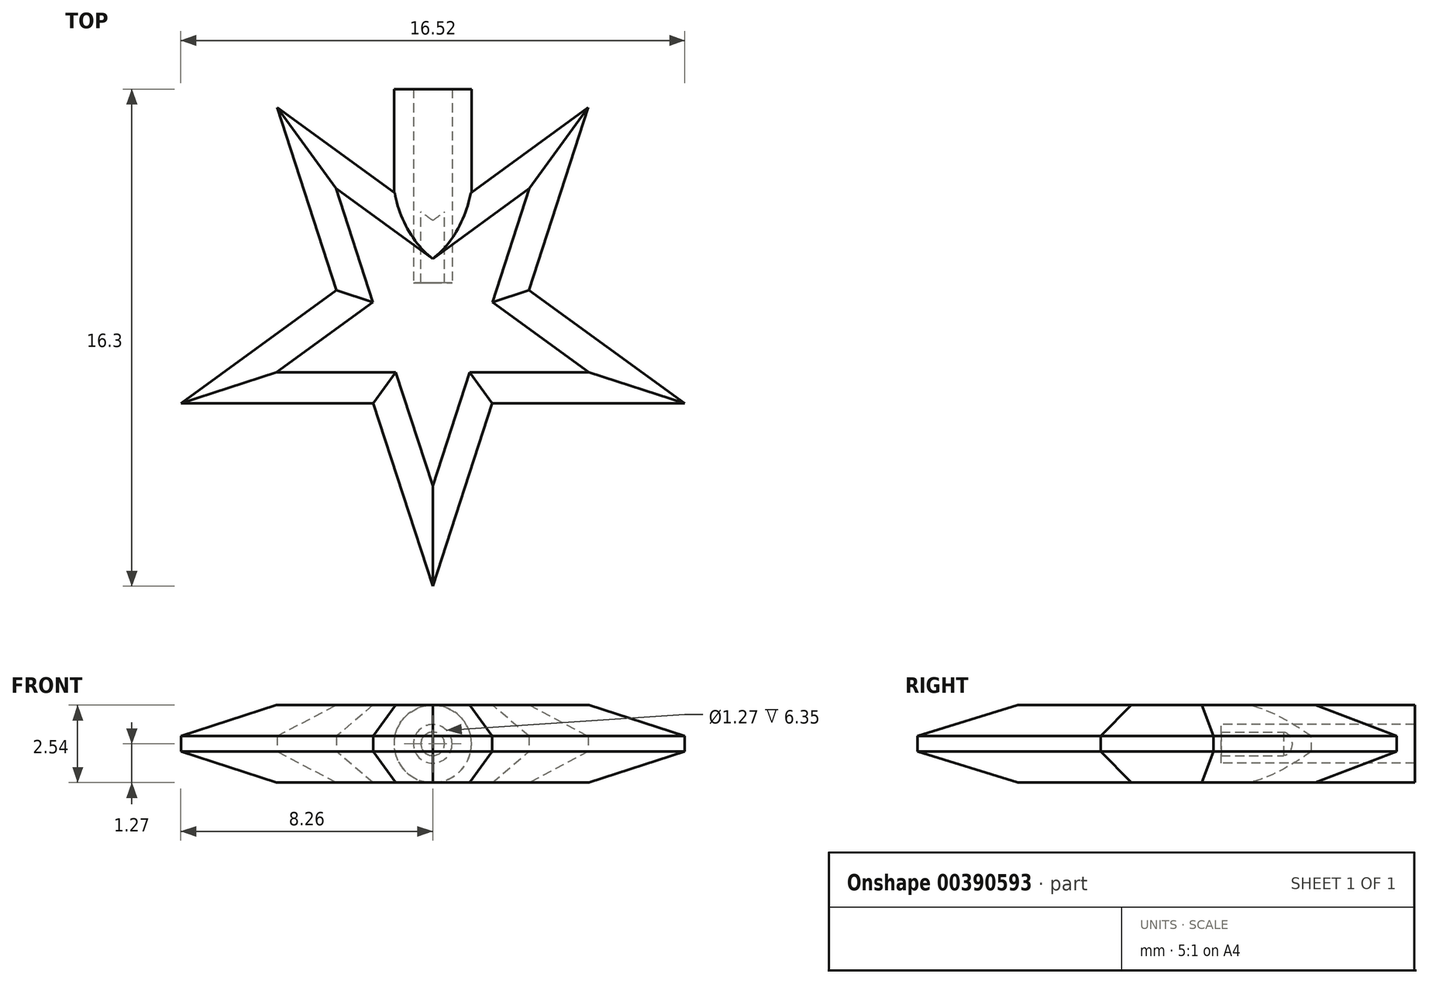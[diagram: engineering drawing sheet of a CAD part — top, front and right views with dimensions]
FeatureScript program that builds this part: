
annotation { "Feature Type Name" : "Feature", "Feature Type Description" : "" }
export const myFeature = defineFeature(function(context is Context, id is Id, definition is map)
    precondition{}
    {
        {
            var Q0;
            Q0=qCreatedBy(makeId("Top.planeOp"),FACE);
            var sketch = newSketch(context, id + "F0", { "sketchPlane" : qUnion([Q0])});
            skCircle(sketch, "E0.cCircle", {"center": v(0, 0) * mm, "radius": 7.02 * mm, "construction": true});
            skLineSegment(sketch, "E0.0", {"start": v(-5.1, 7.02) * mm, "end": v(5.1, 7.02) * mm, "construction": true});
            skLineSegment(sketch, "E0.1", {"start": v(5.1, 7.02) * mm, "end": v(8.26, -2.68) * mm, "construction": true});
            skLineSegment(sketch, "E0.2", {"start": v(8.26, -2.68) * mm, "end": v(0, -8.68) * mm, "construction": true});
            skLineSegment(sketch, "E0.3", {"start": v(0, -8.68) * mm, "end": v(-8.26, -2.68) * mm, "construction": true});
            skLineSegment(sketch, "E0.4", {"start": v(-8.26, -2.68) * mm, "end": v(-5.1, 7.02) * mm, "construction": true});
            skPoint(sketch, "E0.0.midPoint", {"position": v(0, 7.02) * mm});
            skLineSegment(sketch, "E1", {"start": v(-5.1, 7.02) * mm, "end": v(0, -8.68) * mm});
            skLineSegment(sketch, "E2", {"start": v(0, -8.68) * mm, "end": v(5.1, 7.02) * mm});
            skLineSegment(sketch, "E3", {"start": v(5.1, 7.02) * mm, "end": v(-8.26, -2.68) * mm});
            skLineSegment(sketch, "E4", {"start": v(-8.25, -2.68) * mm, "end": v(8.25, -2.68) * mm});
            skLineSegment(sketch, "E5", {"start": v(8.26, -2.68) * mm, "end": v(-5.1, 7.02) * mm});
            skSolve(sketch);
        }
        {
            var Q0;
            Q0 = qSketchRegion(id + "F0", true);
            extrude(context, id + "F1", {"entities" : qUnion([Q0]), "endBound" : BoundingType.SYMMETRIC, "depth" : 2.54 * mm});
        }
        {
            var Q0;
            Q0=qCreatedBy(makeId("Front.planeOp"),FACE);
            var sketch = newSketch(context, id + "F2", { "sketchPlane" : qUnion([Q0])});
            skCircle(sketch, "E6", {"center": v(0, 0) * mm, "radius": 1.27 * mm});
            skCircle(sketch, "E7", {"center": v(0, 0) * mm, "radius": 0.64 * mm});
            skSolve(sketch);
        }
        {
            var Q0;
            Q0 = qSketchRegion(id + "F2", true);
            extrude(context, id + "F3", {"entities" : qUnion([Q0]), "operationType" : NewBodyOperationType.ADD, "oppositeDirection" : true, "depth" : 7.62 * mm});
        }
        {
            var Q0;
            Q0=makeQuery(id+"F3.opExtrude","CAP_FACE",FACE,{"disambiguationData":[OSD([sQuery(id+"F2.wireOp",EDGE,"E6"),sQuery(id+"F2.wireOp",EDGE,"E7")])],"isStart":false});
            var sketch = newSketch(context, id + "F4", { "sketchPlane" : qUnion([Q0])});
            skCircle(sketch, "E8", {"center": v(0, 0) * mm, "radius": 0.39 * mm});
            skSolve(sketch);
        }
        {
            var Q0;
            Q0=makeQuery(id+"F4.imprint","IMPRINT",FACE,{"disambiguationData":[TD([[makeQuery(id+"F4.imprint","IMPRINT",EDGE,{"derivedFrom":makeQuery(id+"F3.opExtrude","CAP_EDGE",EDGE,{"disambiguationData":[OSD([sQuery(id+"F2.wireOp",EDGE,"E7")])],"isStart":false})}),-1.0]])]});
            extrude(context, id + "F5", {"entities" : qUnion([Q0]), "operationType" : NewBodyOperationType.REMOVE, "oppositeDirection" : true, "depth" : 6.35 * mm});
        }
        {
            var Q0;
            Q0=makeQuery(id+"F1.opExtrude","CAP_FACE",FACE,{"disambiguationData":[OSD([sQuery(id+"F0.wireOp",EDGE,"E1"),sQuery(id+"F0.wireOp",EDGE,"E2"),sQuery(id+"F0.wireOp",EDGE,"E3"),sQuery(id+"F0.wireOp",EDGE,"E4"),sQuery(id+"F0.wireOp",EDGE,"E5")])],"isStart":false});
            chamfer(context, id + "F6", {"entities" : qUnion([Q0]), "width" : 1.02 * mm, "tangentPropagation" : true});
        }
        {
            var Q0;
            Q0=makeQuery(id+"F1.opExtrude","CAP_FACE",FACE,{"disambiguationData":[OSD([sQuery(id+"F0.wireOp",EDGE,"E1"),sQuery(id+"F0.wireOp",EDGE,"E2"),sQuery(id+"F0.wireOp",EDGE,"E3"),sQuery(id+"F0.wireOp",EDGE,"E4"),sQuery(id+"F0.wireOp",EDGE,"E5")])],"isStart":true});
            chamfer(context, id + "F7", {"entities" : qUnion([Q0]), "width" : 1.02 * mm, "tangentPropagation" : true});
        }
    });
